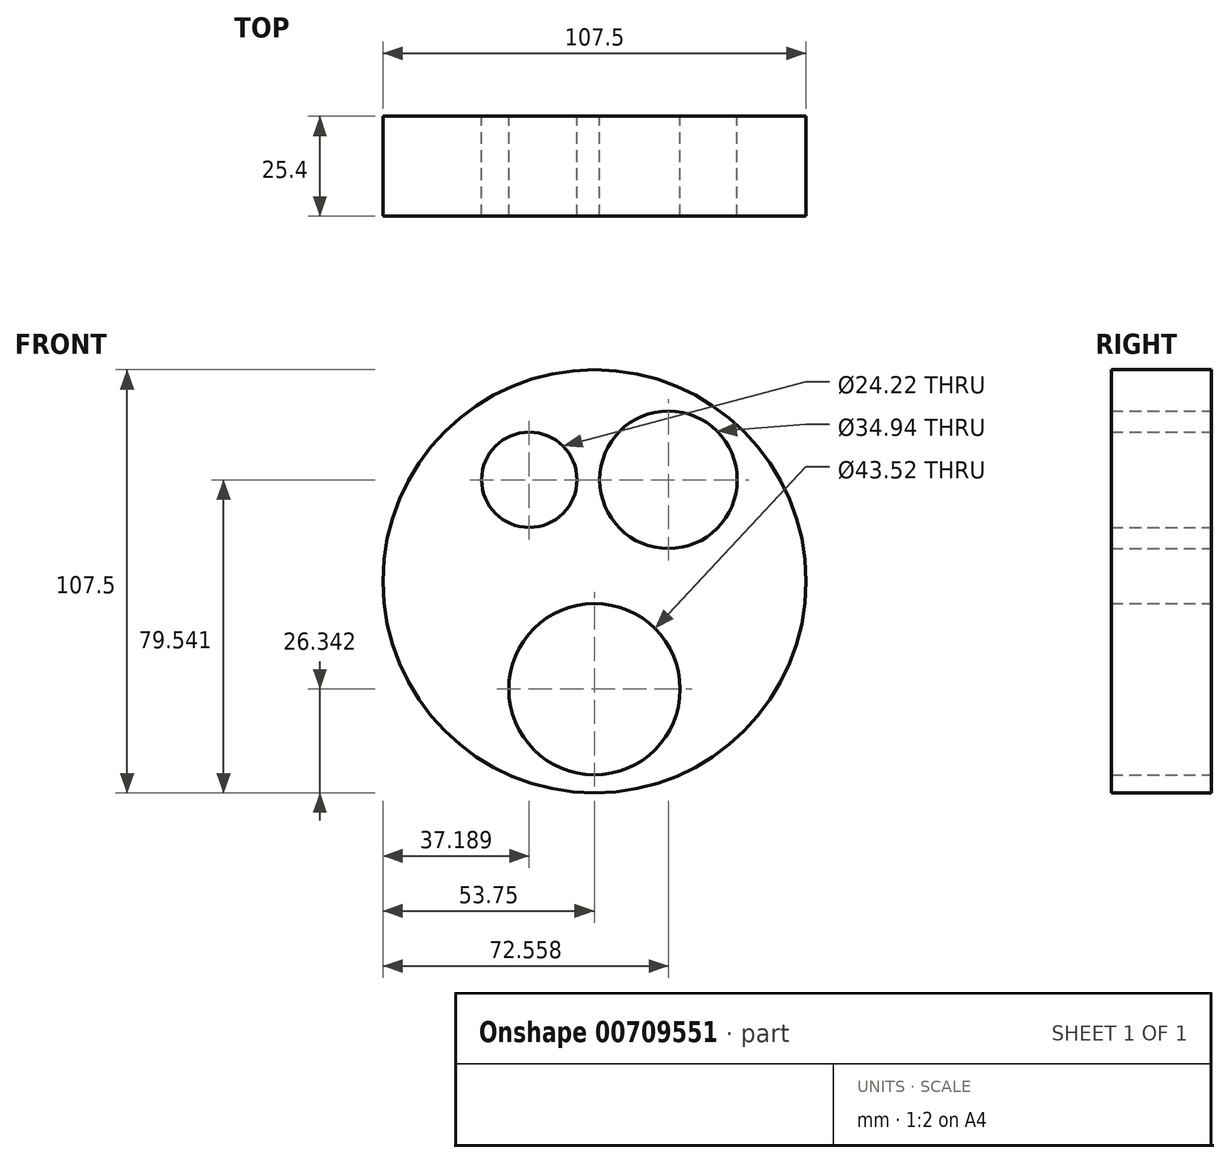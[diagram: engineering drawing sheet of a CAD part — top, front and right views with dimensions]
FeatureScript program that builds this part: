
annotation { "Feature Type Name" : "Feature", "Feature Type Description" : "" }
export const myFeature = defineFeature(function(context is Context, id is Id, definition is map)
    precondition{}
    {
        {
            var Q0;
            Q0=qCreatedBy(makeId("Front.planeOp"),FACE);
            var sketch = newSketch(context, id + "F0", { "sketchPlane" : qUnion([Q0])});
            skCircle(sketch, "E0", {"center": v(0, 0) * mm, "radius": 53.75 * mm});
            skCircle(sketch, "E1", {"center": v(-16.56, 25.8) * mm, "radius": 12.11 * mm});
            skCircle(sketch, "E2", {"center": v(18.8, 25.8) * mm, "radius": 17.47 * mm});
            skCircle(sketch, "E3", {"center": v(0, -27.4) * mm, "radius": 21.76 * mm});
            skSolve(sketch);
        }
        {
            var Q0;
            Q0=makeQuery(id+"F0.imprint","IMPRINT",FACE,{"disambiguationData":[TD([[makeQuery(id+"F0.imprint","IMPRINT",EDGE,{"derivedFrom":sQuery(id+"F0.wireOp",EDGE,"E0")}),1.0]])]});
            extrude(context, id + "F1", {"entities" : qUnion([Q0]), "depth" : 25.4 * mm, "offsetDistance" : 25.4 * mm});
        }
    });
